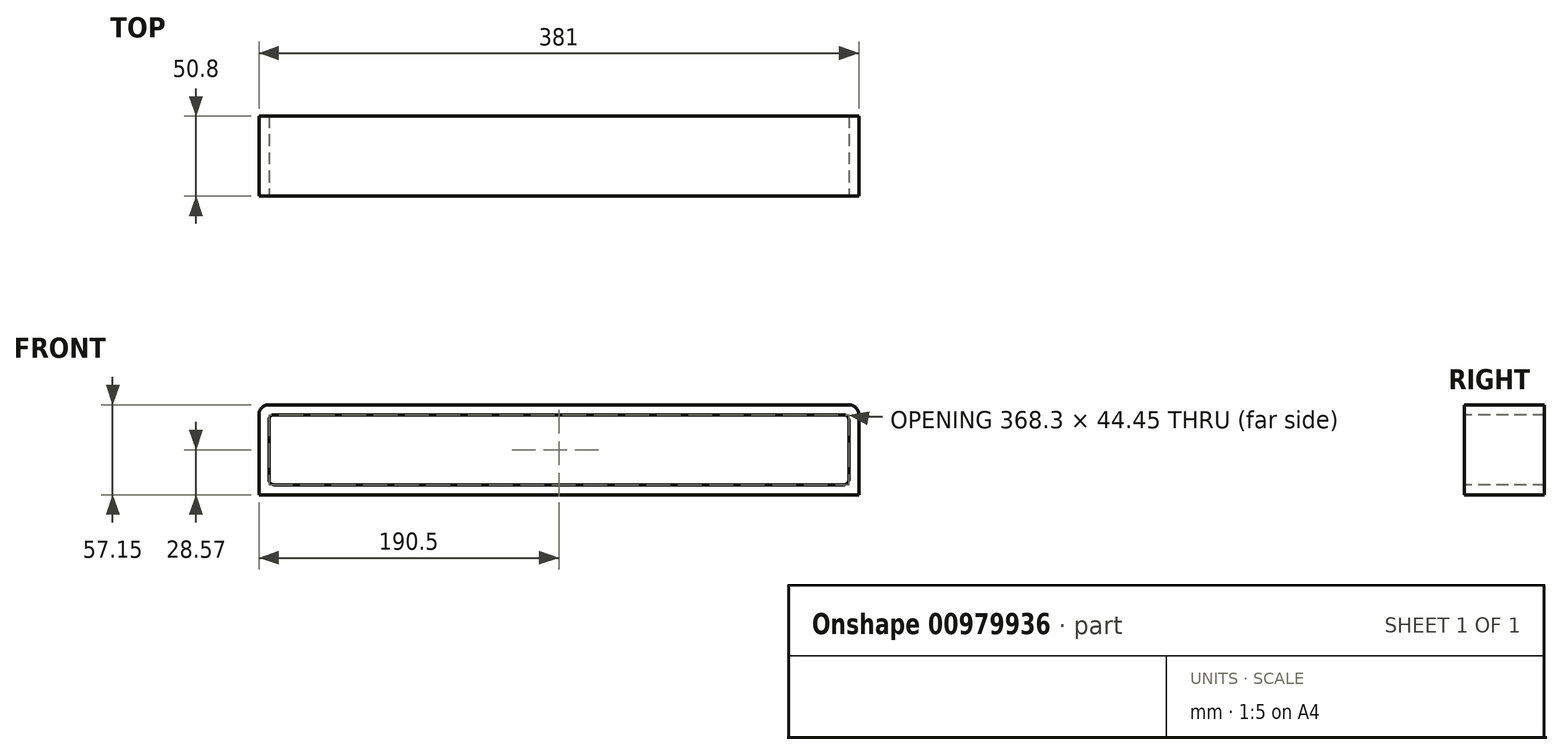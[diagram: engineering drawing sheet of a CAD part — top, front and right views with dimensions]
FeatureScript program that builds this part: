
annotation { "Feature Type Name" : "Feature", "Feature Type Description" : "" }
export const myFeature = defineFeature(function(context is Context, id is Id, definition is map)
    precondition{}
    {
        {
            var Q0;
            Q0=qCreatedBy(makeId("Front.planeOp"),FACE);
            var sketch = newSketch(context, id + "F0", { "sketchPlane" : qUnion([Q0])});
            skLineSegment(sketch, "E0.bottom", {"start": v(190.5, -28.57) * mm, "end": v(-190.5, -28.58) * mm});
            skLineSegment(sketch, "E0.top", {"start": v(190.5, 28.58) * mm, "end": v(-190.5, 28.57) * mm});
            skLineSegment(sketch, "E0.left", {"start": v(190.5, -28.57) * mm, "end": v(190.5, 28.58) * mm});
            skLineSegment(sketch, "E0.right", {"start": v(-190.5, -28.58) * mm, "end": v(-190.5, 28.57) * mm});
            skPoint(sketch, "E0.middle", {"position": v(0, 0) * mm});
            skSolve(sketch);
        }
        {
            var Q0;
            Q0=makeQuery(id+"F0.imprint","IMPRINT",FACE,{"disambiguationData":[TD([[makeQuery(id+"F0.imprint","IMPRINT",EDGE,{"derivedFrom":sQuery(id+"F0.wireOp",EDGE,"E0.bottom")}),-1.0]])]});
            extrude(context, id + "F1", {"entities" : qUnion([Q0]), "depth" : 50.8 * mm, "offsetDistance" : 25.4 * mm});
        }
        {
            var Q0;
            Q0=makeQuery(id+"F1.opExtrude","SWEPT_EDGE",EDGE,{"disambiguationData":[OSD([sQuery(id+"F0.wireOp",EDGE,"E0.top"),sQuery(id+"F0.wireOp",EDGE,"E0.left")])]});
            var Q1;
            Q1=makeQuery(id+"F1.opExtrude","SWEPT_EDGE",EDGE,{"disambiguationData":[OSD([sQuery(id+"F0.wireOp",EDGE,"E0.top"),sQuery(id+"F0.wireOp",EDGE,"E0.right")])]});
            fillet(context, id + "F2", {"entities" : qUnion([Q0, Q1]), "radius" : 6.35 * mm, "tangentPropagation" : true, "allowEdgeOverflow" : false});
        }
        {
            var Q0;
            Q0=makeQuery(id+"F1.opExtrude","SWEPT_BODY",BODY,{"disambiguationData":[OSD([sQuery(id+"F0.wireOp",EDGE,"E0.bottom"),sQuery(id+"F0.wireOp",EDGE,"E0.top"),sQuery(id+"F0.wireOp",EDGE,"E0.left"),sQuery(id+"F0.wireOp",EDGE,"E0.right")])]});
            transform(context, id + "F3", {"entities" : qUnion([Q0]), "transformType" : TransformType.TRANSLATION_3D, "dx" : 0 * mm, "dy" : 50.8 * mm, "dz" : 0 * mm, "makeCopy" : false});
        }
        {
            var Q0;
            Q0=qCreatedBy(makeId("Front.planeOp"),FACE);
            var sketch = newSketch(context, id + "F4", { "sketchPlane" : qUnion([Q0])});
            skLineSegment(sketch, "E1.bottom", {"start": v(184.15, -22.22) * mm, "end": v(-184.15, -22.23) * mm});
            skLineSegment(sketch, "E1.top", {"start": v(184.15, 22.23) * mm, "end": v(-184.15, 22.22) * mm});
            skLineSegment(sketch, "E1.left", {"start": v(184.15, -22.22) * mm, "end": v(184.15, 22.23) * mm});
            skLineSegment(sketch, "E1.right", {"start": v(-184.15, -22.23) * mm, "end": v(-184.15, 22.22) * mm});
            skPoint(sketch, "E1.middle", {"position": v(0, 0) * mm});
            skSolve(sketch);
        }
        {
            var Q0;
            Q0=makeQuery(id+"F4.imprint","IMPRINT",FACE,{"disambiguationData":[TD([[makeQuery(id+"F4.imprint","IMPRINT",EDGE,{"derivedFrom":sQuery(id+"F4.wireOp",EDGE,"E1.bottom")}),-1.0]])]});
            extrude(context, id + "F5", {"entities" : qUnion([Q0]), "operationType" : NewBodyOperationType.REMOVE, "oppositeDirection" : true, "depth" : 50.8 * mm, "offsetDistance" : 25.4 * mm});
        }
        {
            var Q0;
            Q0=makeQuery(id+"F5.boolean.opBoolean","COPY",EDGE,{"derivedFrom":makeQuery(id+"F5.opExtrude","SWEPT_EDGE",EDGE,{"disambiguationData":[OSD([sQuery(id+"F4.wireOp",EDGE,"E1.bottom"),sQuery(id+"F4.wireOp",EDGE,"E1.left")])]})});
            var Q1;
            Q1=makeQuery(id+"F5.boolean.opBoolean","COPY",EDGE,{"derivedFrom":makeQuery(id+"F5.opExtrude","SWEPT_EDGE",EDGE,{"disambiguationData":[OSD([sQuery(id+"F4.wireOp",EDGE,"E1.top"),sQuery(id+"F4.wireOp",EDGE,"E1.left")])]})});
            var Q2;
            Q2=makeQuery(id+"F5.boolean.opBoolean","COPY",EDGE,{"derivedFrom":makeQuery(id+"F5.opExtrude","SWEPT_EDGE",EDGE,{"disambiguationData":[OSD([sQuery(id+"F4.wireOp",EDGE,"E1.top"),sQuery(id+"F4.wireOp",EDGE,"E1.right")])]})});
            var Q3;
            Q3=makeQuery(id+"F5.boolean.opBoolean","COPY",EDGE,{"derivedFrom":makeQuery(id+"F5.opExtrude","SWEPT_EDGE",EDGE,{"disambiguationData":[OSD([sQuery(id+"F4.wireOp",EDGE,"E1.bottom"),sQuery(id+"F4.wireOp",EDGE,"E1.right")])]})});
            fillet(context, id + "F6", {"entities" : qUnion([Q0, Q1, Q2, Q3]), "radius" : 3.17 * mm, "tangentPropagation" : true, "allowEdgeOverflow" : false});
        }
        {
            var Q0;
            Q0=makeQuery(id+"F1.opExtrude","SWEPT_BODY",BODY,{"disambiguationData":[OSD([sQuery(id+"F0.wireOp",EDGE,"E0.bottom"),sQuery(id+"F0.wireOp",EDGE,"E0.top"),sQuery(id+"F0.wireOp",EDGE,"E0.left"),sQuery(id+"F0.wireOp",EDGE,"E0.right")])]});
            transform(context, id + "F7", {"entities" : qUnion([Q0]), "transformType" : TransformType.TRANSLATION_3D, "dx" : 0 * mm, "dy" : 50.8 * mm, "dz" : 0 * mm, "makeCopy" : false});
        }
        {
            var Q0;
            Q0=makeQuery(id+"F1.opExtrude","SWEPT_BODY",BODY,{"disambiguationData":[OSD([sQuery(id+"F0.wireOp",EDGE,"E0.bottom"),sQuery(id+"F0.wireOp",EDGE,"E0.top"),sQuery(id+"F0.wireOp",EDGE,"E0.left"),sQuery(id+"F0.wireOp",EDGE,"E0.right")])]});
            transform(context, id + "F8", {"entities" : qUnion([Q0]), "transformType" : TransformType.TRANSLATION_3D, "dx" : 0 * mm, "dy" : 0 * mm, "dz" : -101.6 * mm, "makeCopy" : false});
        }
        {
            var Q0;
            Q0=makeQuery(id+"F1.opExtrude","SWEPT_BODY",BODY,{"disambiguationData":[OSD([sQuery(id+"F0.wireOp",EDGE,"E0.bottom"),sQuery(id+"F0.wireOp",EDGE,"E0.top"),sQuery(id+"F0.wireOp",EDGE,"E0.left"),sQuery(id+"F0.wireOp",EDGE,"E0.right")])]});
            transform(context, id + "F9", {"entities" : qUnion([Q0]), "transformType" : TransformType.TRANSLATION_3D, "dx" : 0 * mm, "dy" : 50.8 * mm, "dz" : 50.8 * mm, "makeCopy" : false});
        }
        {
            var Q0;
            Q0=makeQuery(id+"F1.opExtrude","SWEPT_BODY",BODY,{"disambiguationData":[OSD([sQuery(id+"F0.wireOp",EDGE,"E0.bottom"),sQuery(id+"F0.wireOp",EDGE,"E0.top"),sQuery(id+"F0.wireOp",EDGE,"E0.left"),sQuery(id+"F0.wireOp",EDGE,"E0.right")])]});
            transform(context, id + "F10", {"entities" : qUnion([Q0]), "transformType" : TransformType.TRANSLATION_3D, "dx" : 0 * mm, "dy" : 50.8 * mm, "dz" : 50.8 * mm, "makeCopy" : false});
        }
    });
